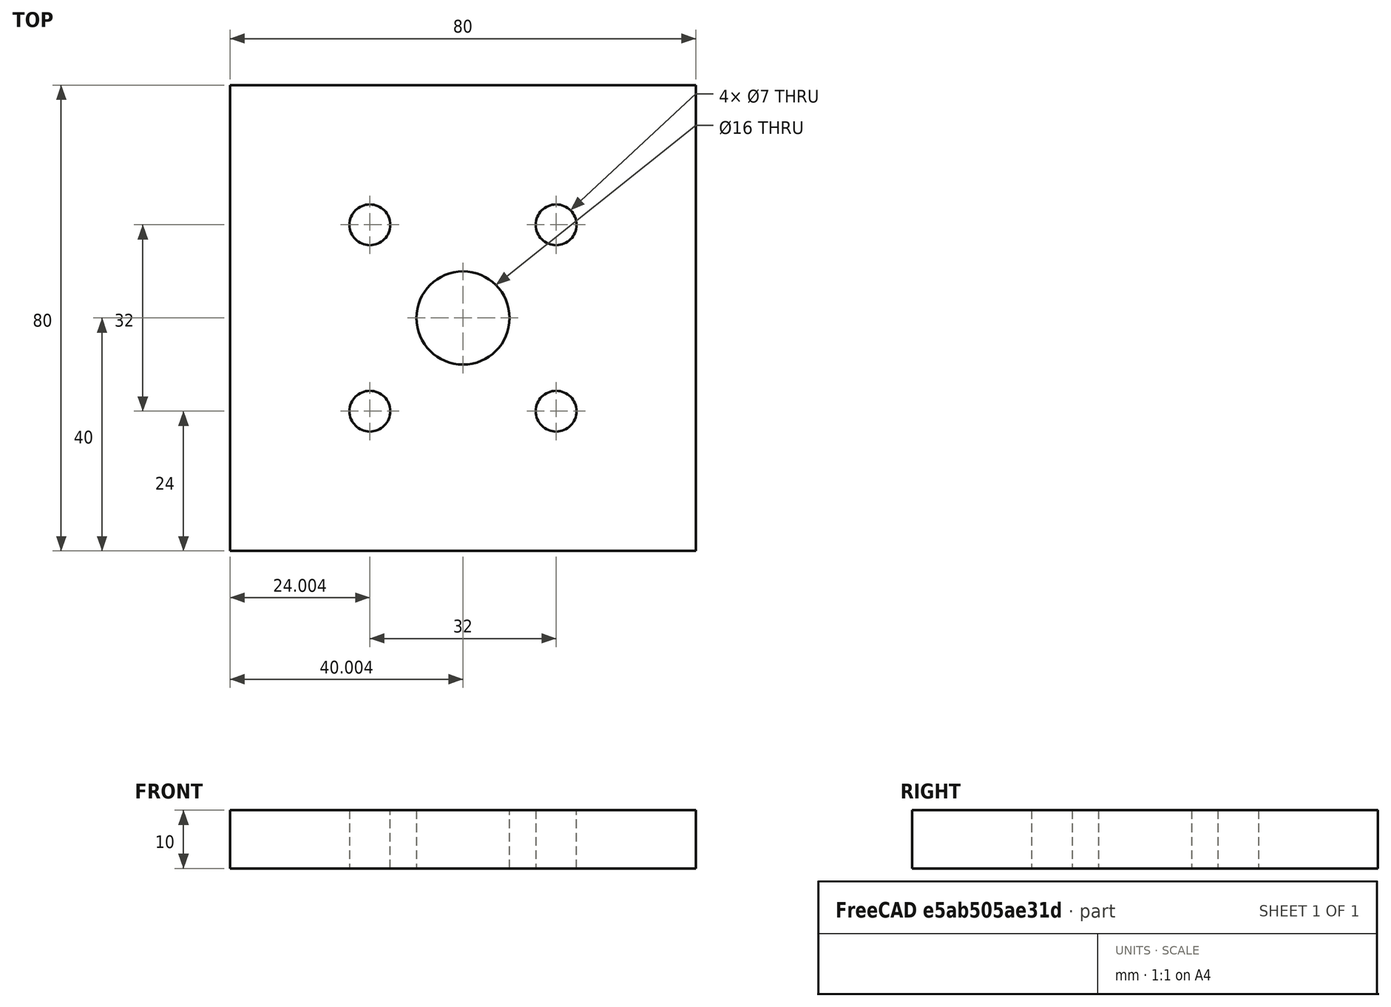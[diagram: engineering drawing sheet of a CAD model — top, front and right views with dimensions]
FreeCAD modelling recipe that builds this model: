
FCSTD DOCUMENT
Label: BasicFreeCAD Bearing plate
objects: Sketcher::SketchObject×1, PartDesign::Pad×1
note: 3 computed .brp shape members not serialized (recipe doc carries the construction recipe); baked Part::Feature solids carry a one-line shape summary decoded from their .brp

FEATURE [Sketcher::SketchObject] Sketch
  sketch-geometry (9):
    g0: LineSegment StartX=-80.116 StartY=40 StartZ=0 EndX=-0.115967 EndY=40 EndZ=0
    g1: LineSegment StartX=-0.115967 StartY=40 StartZ=0 EndX=-0.115967 EndY=-40 EndZ=0
    g2: LineSegment StartX=-0.115967 StartY=-40 StartZ=0 EndX=-80.116 EndY=-40 EndZ=0
    g3: LineSegment StartX=-80.116 StartY=-40 StartZ=0 EndX=-80.116 EndY=40 EndZ=0
    g4: Circle CenterX=-40.116 CenterY=0 CenterZ=0 NormalX=0 NormalY=0 NormalZ=1 Radius=8
    g5: Circle CenterX=-24.116 CenterY=16 CenterZ=0 NormalX=0 NormalY=0 NormalZ=1 Radius=3.5
    g6: Circle CenterX=-56.116 CenterY=16 CenterZ=0 NormalX=0 NormalY=0 NormalZ=1 Radius=3.5
    g7: Circle CenterX=-56.116 CenterY=-16 CenterZ=0 NormalX=0 NormalY=0 NormalZ=1 Radius=3.5
    g8: Circle CenterX=-24.116 CenterY=-16 CenterZ=0 NormalX=0 NormalY=0 NormalZ=1 Radius=3.5
  constraints (26):
    c: Coincident(g0,g1)
    c: Coincident(g1,g2)
    c: Coincident(g2,g3)
    c: Coincident(g3,g0)
    c: Horizontal(g0)
    c: Horizontal(g2)
    c: Vertical(g1)
    c: Vertical(g3)
    c: DistanceX(g0) = 80
    c: DistanceY(g1) = -80
    c: PointOnObject(g4,g-1)
    c: Radius(g4) = 8
    c: Distance(g4,g3) = 40
    c: Distance(g4,g0) = 40
    c: Distance(g6,g0) = 24
    c: Distance(g6,g3) = 24
    c: Radius(g6) = 3.5
    c: Equal(g5,g6)
    c: Equal(g8,g6)
    c: Equal(g7,g6)
    c: Distance(g5,g0) = 24
    c: Distance(g5,g1) = 24
    c: Distance(g8,g1) = 24
    c: Distance(g8,g2) = 24
    c: Distance(g7,g2) = 24
    c: Distance(g7,g3) = 24
FEATURE [PartDesign::Pad] Pad
  Length = 10
  Length2 = 100
  Sketch = -> Sketch
  Type = 0
